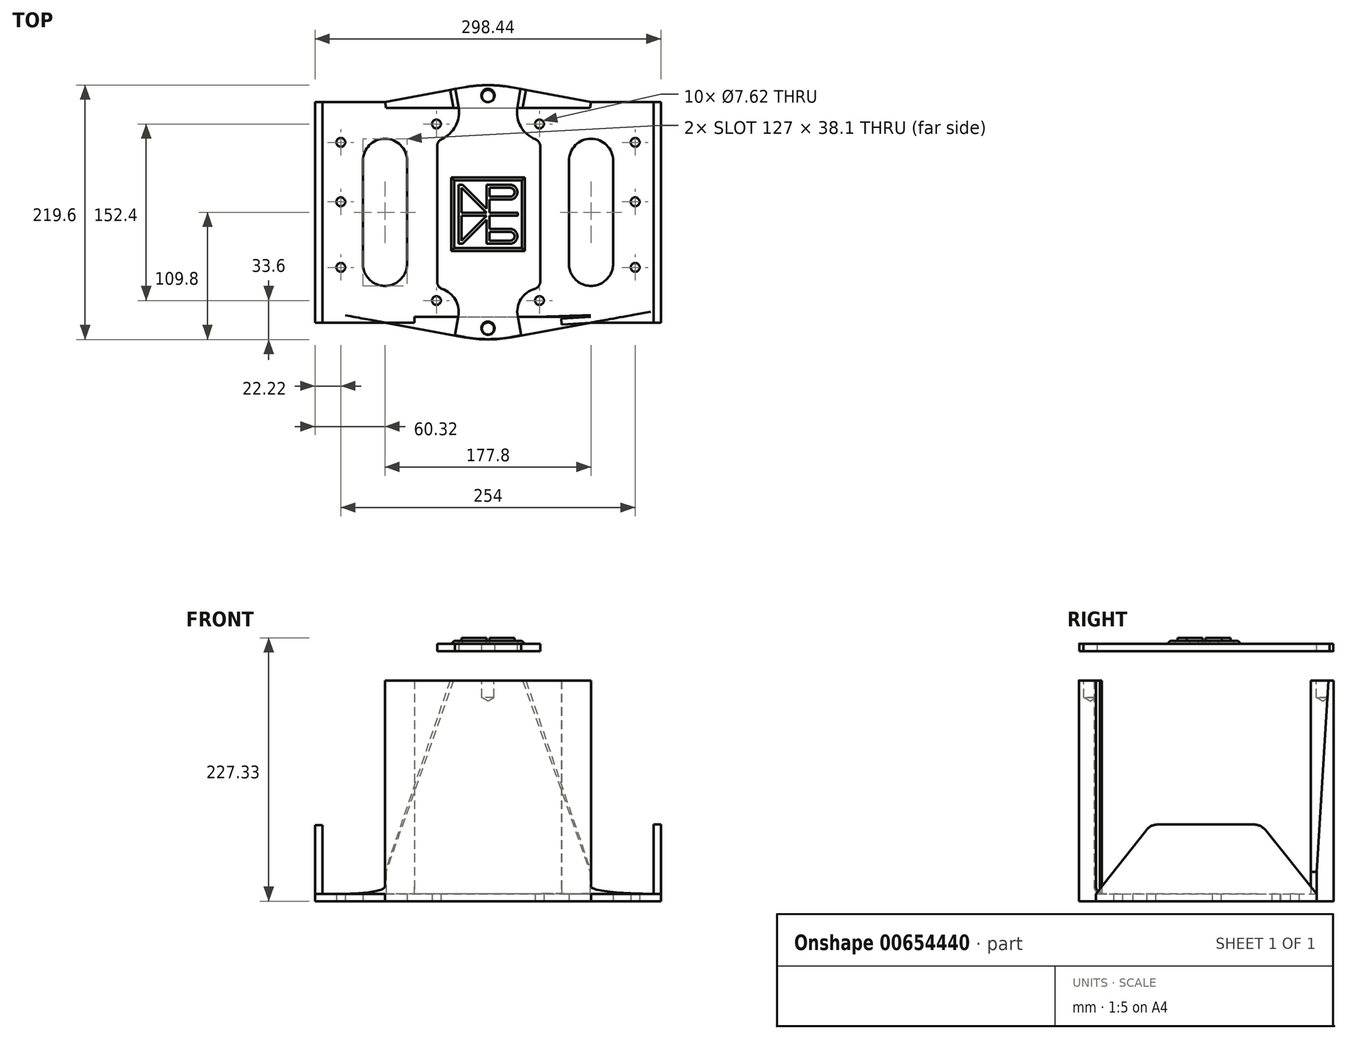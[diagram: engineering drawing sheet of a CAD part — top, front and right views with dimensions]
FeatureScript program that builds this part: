
annotation { "Feature Type Name" : "Feature", "Feature Type Description" : "" }
export const myFeature = defineFeature(function(context is Context, id is Id, definition is map)
    precondition{}
    {
        {
            var Q0;
            Q0=qCreatedBy(makeId("Top.planeOp"),FACE);
            var sketch = newSketch(context, id + "F0", { "sketchPlane" : qUnion([Q0])});
            skLineSegment(sketch, "E0.bottom", {"start": v(-146.05, 86.2) * mm, "end": v(146.05, 86.2) * mm});
            skLineSegment(sketch, "E0.top", {"start": v(-146.05, -104.3) * mm, "end": v(146.05, -104.3) * mm});
            skLineSegment(sketch, "E0.left", {"start": v(-146.05, 86.2) * mm, "end": v(-146.05, -104.3) * mm});
            skLineSegment(sketch, "E0.right", {"start": v(146.05, 86.2) * mm, "end": v(146.05, -104.3) * mm});
            skPoint(sketch, "E1", {"position": v(127, 51.34) * mm});
            skPoint(sketch, "E2", {"position": v(127, -56.61) * mm});
            skPoint(sketch, "E3", {"position": v(127, 0) * mm});
            skPoint(sketch, "E4", {"position": v(-127, 0) * mm});
            skPoint(sketch, "E5", {"position": v(-127, 51.34) * mm});
            skPoint(sketch, "E6", {"position": v(-127, -56.61) * mm});
            skPoint(sketch, "E7", {"position": v(-44.45, 67.14) * mm});
            skPoint(sketch, "E8", {"position": v(44.45, 67.14) * mm});
            skPoint(sketch, "E9", {"position": v(-44.45, -85.26) * mm});
            skPoint(sketch, "E10", {"position": v(44.45, -85.26) * mm});
            skLineSegment(sketch, "E11", {"start": v(-107.95, 35.4) * mm, "end": v(-107.95, -53.5) * mm});
            skLineSegment(sketch, "E12", {"start": v(-69.85, 35.4) * mm, "end": v(-69.85, -53.5) * mm});
            skArc(sketch, "E13", {"start": v(-107.95, 35.4) * mm, "mid": v(-88.9, 54.44) * mm, "end": v(-69.85, 35.4) * mm});
            skArc(sketch, "E14", {"start": v(-107.95, -53.5) * mm, "mid": v(-88.9, -72.56) * mm, "end": v(-69.85, -53.5) * mm});
            skLineSegment(sketch, "E15.MirrorCS", {"start": v(69.85, 35.4) * mm, "end": v(69.85, -53.5) * mm});
            skArc(sketch, "E16.MirrorCS", {"start": v(107.95, 35.4) * mm, "mid": v(88.9, 54.44) * mm, "end": v(69.85, 35.4) * mm});
            skLineSegment(sketch, "E17.MirrorCS", {"start": v(107.95, 35.4) * mm, "end": v(107.95, -53.5) * mm});
            skArc(sketch, "E18.MirrorCS", {"start": v(107.95, -53.5) * mm, "mid": v(88.9, -72.56) * mm, "end": v(69.85, -53.5) * mm});
            skPoint(sketch, "E19", {"position": v(-88.9, 86.2) * mm});
            skPoint(sketch, "E19.positionSnap0", {"position": v(-88.9, 54.44) * mm});
            skPoint(sketch, "E20", {"position": v(-88.9, -104.3) * mm});
            skPoint(sketch, "E20.positionSnap0", {"position": v(-88.9, -72.56) * mm});
            skPoint(sketch, "E21", {"position": v(88.9, 86.2) * mm});
            skPoint(sketch, "E22", {"position": v(88.9, -104.3) * mm});
            skLineSegment(sketch, "E23", {"start": v(-88.9, 86.2) * mm, "end": v(-20.21, 98.9) * mm});
            skLineSegment(sketch, "E24.MirrorCS", {"start": v(88.9, 86.2) * mm, "end": v(20.21, 98.9) * mm});
            skArc(sketch, "E25", {"start": v(-20.21, 98.9) * mm, "mid": v(0, 100.74) * mm, "end": v(20.21, 98.9) * mm});
            skLineSegment(sketch, "E26", {"start": v(-88.9, -104.3) * mm, "end": v(-20.21, -117) * mm});
            skLineSegment(sketch, "E27.MirrorCS", {"start": v(88.9, -104.3) * mm, "end": v(20.21, -117) * mm});
            skArc(sketch, "E28", {"start": v(-20.21, -117) * mm, "mid": v(0, -118.86) * mm, "end": v(20.21, -117) * mm});
            skLineSegment(sketch, "E29", {"start": v(-88.9, -104.3) * mm, "end": v(-88.9, -99.23) * mm});
            skLineSegment(sketch, "E30", {"start": v(-88.9, -99.23) * mm, "end": v(88.59, -99.23) * mm});
            skLineSegment(sketch, "E31", {"start": v(88.59, -99.23) * mm, "end": v(88.9, -104.3) * mm});
            skLineSegment(sketch, "E32", {"start": v(-88.9, 86.2) * mm, "end": v(-88.9, 81.11) * mm});
            skLineSegment(sketch, "E33", {"start": v(-88.9, 81.11) * mm, "end": v(89.2, 81.11) * mm});
            skLineSegment(sketch, "E34", {"start": v(89.2, 81.11) * mm, "end": v(88.9, 86.2) * mm});
            skSolve(sketch);
        }
        {
            var Q0;
            Q0=makeQuery(id+"F0.imprint","IMPRINT",FACE,{"disambiguationData":[TD([[makeQuery(id+"F0.imprint","IMPRINT",EDGE,{"derivedFrom":sQuery(id+"F0.wireOp",EDGE,"E0.bottom")}),-1.0]])]});
            extrude(context, id + "F1", {"entities" : qUnion([Q0]), "depth" : 6.35 * mm, "offsetDistance" : 25.4 * mm});
        }
        {
            var Q0;
            {var subQ0=sQuery(id+"F0.wireOp",EDGE,"E32");Q0=makeQuery(id+"F0.imprint","IMPRINT",FACE,{"disambiguationData":[TD([[makeQuery(id+"F0.imprint","IMPRINT",EDGE,{"derivedFrom":subQ0}),1.0]])]});}
            var Q1;
            {var subQ0=sQuery(id+"F0.wireOp",EDGE,"E23");Q1=makeQuery(id+"F0.imprint","IMPRINT",FACE,{"disambiguationData":[TD([[makeQuery(id+"F0.imprint","IMPRINT",EDGE,{"derivedFrom":subQ0}),-1.0]])]});}
            var Q2;
            {var subQ0=sQuery(id+"F0.wireOp",EDGE,"E29");Q2=makeQuery(id+"F0.imprint","IMPRINT",FACE,{"disambiguationData":[TD([[makeQuery(id+"F0.imprint","IMPRINT",EDGE,{"derivedFrom":subQ0}),-1.0]])]});}
            var Q3;
            {var subQ0=sQuery(id+"F0.wireOp",EDGE,"E26");Q3=makeQuery(id+"F0.imprint","IMPRINT",FACE,{"disambiguationData":[TD([[makeQuery(id+"F0.imprint","IMPRINT",EDGE,{"derivedFrom":subQ0}),1.0]])]});}
            extrude(context, id + "F2", {"entities" : qUnion([Q0, Q1, Q2, Q3]), "operationType" : NewBodyOperationType.ADD, "depth" : 190.5 * mm, "offsetDistance" : 25.4 * mm});
        }
        {
            var Q0;
            Q0=makeQuery(id+"F1.opExtrude","CAP_FACE",FACE,{"disambiguationData":[OSD([sQuery(id+"F0.wireOp",EDGE,"E0.bottom"),sQuery(id+"F0.wireOp",EDGE,"E0.top"),sQuery(id+"F0.wireOp",EDGE,"E0.left"),sQuery(id+"F0.wireOp",EDGE,"E0.right"),sQuery(id+"F0.wireOp",EDGE,"E11"),sQuery(id+"F0.wireOp",EDGE,"E12"),sQuery(id+"F0.wireOp",EDGE,"E13"),sQuery(id+"F0.wireOp",EDGE,"E14"),sQuery(id+"F0.wireOp",EDGE,"E15.MirrorCS"),sQuery(id+"F0.wireOp",EDGE,"E16.MirrorCS"),sQuery(id+"F0.wireOp",EDGE,"E17.MirrorCS"),sQuery(id+"F0.wireOp",EDGE,"E18.MirrorCS")])],"isStart":false});
            var sketch = newSketch(context, id + "F3", { "sketchPlane" : qUnion([Q0])});
            skLineSegment(sketch, "E35.bottom", {"start": v(-140.97, 81.11) * mm, "end": v(140.97, 81.11) * mm});
            skLineSegment(sketch, "E35.top", {"start": v(-140.97, -99.23) * mm, "end": v(140.97, -99.23) * mm});
            skLineSegment(sketch, "E35.left", {"start": v(-140.97, 81.11) * mm, "end": v(-140.97, -99.23) * mm});
            skLineSegment(sketch, "E35.right", {"start": v(140.97, 81.11) * mm, "end": v(140.97, -99.23) * mm});
            skLineSegment(sketch, "E36.bottom", {"start": v(-146.05, 86.2) * mm, "end": v(146.05, 86.2) * mm});
            skLineSegment(sketch, "E36.top", {"start": v(-146.05, -104.3) * mm, "end": v(146.05, -104.3) * mm});
            skLineSegment(sketch, "E36.left", {"start": v(-146.05, 86.2) * mm, "end": v(-146.05, -104.3) * mm});
            skLineSegment(sketch, "E36.right", {"start": v(146.05, 86.2) * mm, "end": v(146.05, -104.3) * mm});
            skSolve(sketch);
        }
        {
            var Q0;
            Q0=makeQuery(id+"F3.imprint","IMPRINT",FACE,{"disambiguationData":[TD([[makeQuery(id+"F3.imprint","IMPRINT",EDGE,{"derivedFrom":sQuery(id+"F3.wireOp",EDGE,"E35.bottom")}),1.0]])]});
            extrude(context, id + "F4", {"entities" : qUnion([Q0]), "operationType" : NewBodyOperationType.ADD, "depth" : 25.4 * mm, "offsetDistance" : 25.4 * mm});
        }
        {
            var Q0;
            Q0=sQuery(id+"F0.wireOp",VERTEX,"E5");
            var Q1;
            Q1=sQuery(id+"F0.wireOp",VERTEX,"E4");
            var Q2;
            Q2=sQuery(id+"F0.wireOp",VERTEX,"E6");
            var Q3;
            Q3=sQuery(id+"F0.wireOp",VERTEX,"E9");
            var Q4;
            Q4=sQuery(id+"F0.wireOp",VERTEX,"E10");
            var Q5;
            Q5=sQuery(id+"F0.wireOp",VERTEX,"E2");
            var Q6;
            Q6=sQuery(id+"F0.wireOp",VERTEX,"E3");
            var Q7;
            Q7=sQuery(id+"F0.wireOp",VERTEX,"E1");
            var Q8;
            Q8=sQuery(id+"F0.wireOp",VERTEX,"E8");
            var Q9;
            Q9=sQuery(id+"F0.wireOp",VERTEX,"E7");
            var Q10;
            Q10=makeQuery(id+"F1.opExtrude","SWEPT_BODY",BODY,{"disambiguationData":[OSD([sQuery(id+"F0.wireOp",EDGE,"E0.bottom"),sQuery(id+"F0.wireOp",EDGE,"E0.top"),sQuery(id+"F0.wireOp",EDGE,"E0.left"),sQuery(id+"F0.wireOp",EDGE,"E0.right"),sQuery(id+"F0.wireOp",EDGE,"E11"),sQuery(id+"F0.wireOp",EDGE,"E12"),sQuery(id+"F0.wireOp",EDGE,"E13"),sQuery(id+"F0.wireOp",EDGE,"E14"),sQuery(id+"F0.wireOp",EDGE,"E15.MirrorCS"),sQuery(id+"F0.wireOp",EDGE,"E16.MirrorCS"),sQuery(id+"F0.wireOp",EDGE,"E17.MirrorCS"),sQuery(id+"F0.wireOp",EDGE,"E18.MirrorCS")])]});
            hole(context, id + "F5", {"style" : HoleStyle.SIMPLE, "endStyle" : HoleEndStyle.THROUGH, "oppositeDirection" : true, "holeDiameter" : 7.62 * mm, "majorDiameter" : 6.35 * mm, "isTappedThrough" : true, "tappedDepth" : 10.16 * mm, "tapClearance" : 3, "locations" : qUnion([Q0, Q1, Q2, Q3, Q4, Q5, Q6, Q7, Q8, Q9]), "scope" : qUnion([Q10])});
        }
        {
            var Q0;
            Q0=makeQuery(id+"F2.opExtrude","SWEPT_FACE",FACE,{"disambiguationData":[OSD([sQuery(id+"F0.wireOp",EDGE,"E26")])]});
            var sketch = newSketch(context, id + "F6", { "sketchPlane" : qUnion([Q0])});
            skLineSegment(sketch, "E37", {"start": v(-68.45, 25.4) * mm, "end": v(-11.3, 190.5) * mm});
            skSolve(sketch);
        }
        {
            var Q0;
            Q0 = qSketchRegion(id + "F6", true);
            var Q1;
            {var subQ0=sQuery(id+"F6.wireOp",EDGE,"E37");Q1=makeQuery(id+"F6.imprint","IMPRINT",FACE,{"disambiguationData":[TD([[makeQuery(id+"F6.imprint","IMPRINT",EDGE,{"derivedFrom":subQ0}),1.0]])]});}
            var Q2;
            Q2=makeQuery(id+"F2.opExtrude","SWEPT_FACE",FACE,{"disambiguationData":[OSD([sQuery(id+"F0.wireOp",EDGE,"E29")])]});
            extrude(context, id + "F7", {"entities" : qUnion([Q0, Q1, Q2]), "operationType" : NewBodyOperationType.REMOVE, "oppositeDirection" : true, "depth" : 25.4 * mm, "offsetDistance" : 25.4 * mm});
        }
        {
            var Q0;
            Q0=makeQuery(id+"F2.opExtrude","SWEPT_FACE",FACE,{"disambiguationData":[OSD([sQuery(id+"F0.wireOp",EDGE,"E27.MirrorCS")])]});
            var sketch = newSketch(context, id + "F8", { "sketchPlane" : qUnion([Q0])});
            skLineSegment(sketch, "E38", {"start": v(11.3, 190.5) * mm, "end": v(68.45, 25.4) * mm});
            skSolve(sketch);
        }
        {
            var Q0;
            Q0 = qSketchRegion(id + "F8", true);
            var Q1;
            {var subQ0=sQuery(id+"F8.wireOp",EDGE,"E38");Q1=makeQuery(id+"F8.imprint","IMPRINT",FACE,{"disambiguationData":[TD([[makeQuery(id+"F8.imprint","IMPRINT",EDGE,{"derivedFrom":subQ0}),1.0]])]});}
            var Q2;
            Q2=makeQuery(id+"F2.opExtrude","SWEPT_FACE",FACE,{"disambiguationData":[OSD([sQuery(id+"F0.wireOp",EDGE,"E31")])]});
            extrude(context, id + "F9", {"entities" : qUnion([Q0, Q1, Q2]), "operationType" : NewBodyOperationType.REMOVE, "oppositeDirection" : true, "depth" : 25.4 * mm, "offsetDistance" : 25.4 * mm});
        }
        {
            var Q0;
            Q0=makeQuery(id+"F2.opExtrude","SWEPT_FACE",FACE,{"disambiguationData":[OSD([sQuery(id+"F0.wireOp",EDGE,"E24.MirrorCS")])]});
            var sketch = newSketch(context, id + "F10", { "sketchPlane" : qUnion([Q0])});
            skLineSegment(sketch, "E39", {"start": v(-14.6, 190.5) * mm, "end": v(-71.75, 25.4) * mm});
            skSolve(sketch);
        }
        {
            var Q0;
            Q0 = qSketchRegion(id + "F10", true);
            var Q1;
            {var subQ0=sQuery(id+"F10.wireOp",EDGE,"E39");Q1=makeQuery(id+"F10.imprint","IMPRINT",FACE,{"disambiguationData":[TD([[makeQuery(id+"F10.imprint","IMPRINT",EDGE,{"derivedFrom":subQ0}),-1.0]])]});}
            var Q2;
            Q2=makeQuery(id+"F2.opExtrude","SWEPT_FACE",FACE,{"disambiguationData":[OSD([sQuery(id+"F0.wireOp",EDGE,"E34")])]});
            extrude(context, id + "F11", {"entities" : qUnion([Q0, Q1, Q2]), "operationType" : NewBodyOperationType.REMOVE, "oppositeDirection" : true, "depth" : 25.4 * mm, "offsetDistance" : 25.4 * mm});
        }
        {
            var Q0;
            Q0=makeQuery(id+"F2.opExtrude","SWEPT_FACE",FACE,{"disambiguationData":[OSD([sQuery(id+"F0.wireOp",EDGE,"E23")])]});
            var sketch = newSketch(context, id + "F12", { "sketchPlane" : qUnion([Q0])});
            skLineSegment(sketch, "E40", {"start": v(14.6, 190.5) * mm, "end": v(71.75, 25.4) * mm});
            skSolve(sketch);
        }
        {
            var Q0;
            Q0 = qSketchRegion(id + "F12", true);
            var Q1;
            {var subQ0=sQuery(id+"F12.wireOp",EDGE,"E40");Q1=makeQuery(id+"F12.imprint","IMPRINT",FACE,{"disambiguationData":[TD([[makeQuery(id+"F12.imprint","IMPRINT",EDGE,{"derivedFrom":subQ0}),1.0]])]});}
            var Q2;
            Q2=makeQuery(id+"F2.opExtrude","SWEPT_FACE",FACE,{"disambiguationData":[OSD([sQuery(id+"F0.wireOp",EDGE,"E32")])]});
            extrude(context, id + "F13", {"entities" : qUnion([Q0, Q1, Q2]), "operationType" : NewBodyOperationType.REMOVE, "oppositeDirection" : true, "depth" : 25.4 * mm, "offsetDistance" : 25.4 * mm});
        }
        {
            var Q0;
            Q0=makeQuery(id+"F1.opExtrude","SWEPT_FACE",FACE,{"disambiguationData":[OSD([sQuery(id+"F0.wireOp",EDGE,"E0.left")])]});
            var sketch = newSketch(context, id + "F14", { "sketchPlane" : qUnion([Q0])});
            skLineSegment(sketch, "E41", {"start": v(-86.2, 0) * mm, "end": v(-86.2, 6.35) * mm});
            skLineSegment(sketch, "E42", {"start": v(-86.2, 6.35) * mm, "end": v(-42.22, 60.97) * mm});
            skLineSegment(sketch, "E43", {"start": v(-32.33, 65.7) * mm, "end": v(50.74, 65.7) * mm});
            skLineSegment(sketch, "E44", {"start": v(60.65, 60.94) * mm, "end": v(104.3, 6.35) * mm});
            skLineSegment(sketch, "E45", {"start": v(104.3, 6.35) * mm, "end": v(104.3, 0) * mm});
            skLineSegment(sketch, "E46", {"start": v(104.3, 0) * mm, "end": v(-86.2, 0) * mm});
            skPoint(sketch, "E47.visualSharp", {"position": v(-38.4, 65.7) * mm});
            skArc(sketch, "E47.filletArc", {"start": v(-32.33, 65.7) * mm, "mid": v(-37.81, 64.46) * mm, "end": v(-42.22, 60.97) * mm});
            skPoint(sketch, "E48.visualSharp", {"position": v(56.84, 65.7) * mm});
            skArc(sketch, "E48.filletArc", {"start": v(60.65, 60.94) * mm, "mid": v(56.24, 64.45) * mm, "end": v(50.74, 65.7) * mm});
            skSolve(sketch);
        }
        {
            var Q0;
            Q0 = qSketchRegion(id + "F14", true);
            extrude(context, id + "F15", {"entities" : qUnion([Q0]), "operationType" : NewBodyOperationType.ADD, "endBound" : BoundingType.SYMMETRIC, "depth" : 6.35 * mm, "offsetDistance" : 25.4 * mm});
        }
        {
            var Q0;
            Q0=makeQuery(id+"F1.opExtrude","SWEPT_FACE",FACE,{"disambiguationData":[OSD([sQuery(id+"F0.wireOp",EDGE,"E0.right")])]});
            var sketch = newSketch(context, id + "F16", { "sketchPlane" : qUnion([Q0])});
            skLineSegment(sketch, "E49", {"start": v(-104.3, 0) * mm, "end": v(-104.3, 6.35) * mm});
            skLineSegment(sketch, "E50", {"start": v(-104.3, 6.35) * mm, "end": v(-60.88, 61.31) * mm});
            skLineSegment(sketch, "E51", {"start": v(-50.92, 66.14) * mm, "end": v(32.09, 66.14) * mm});
            skLineSegment(sketch, "E52", {"start": v(42, 61.4) * mm, "end": v(86.2, 6.35) * mm});
            skLineSegment(sketch, "E53", {"start": v(86.2, 6.35) * mm, "end": v(86.2, 0) * mm});
            skLineSegment(sketch, "E54", {"start": v(86.2, 0) * mm, "end": v(-104.3, 0) * mm});
            skPoint(sketch, "E55.visualSharp", {"position": v(-57.07, 66.14) * mm});
            skArc(sketch, "E55.filletArc", {"start": v(-50.92, 66.14) * mm, "mid": v(-56.46, 64.87) * mm, "end": v(-60.88, 61.31) * mm});
            skPoint(sketch, "E56.visualSharp", {"position": v(38.18, 66.14) * mm});
            skArc(sketch, "E56.filletArc", {"start": v(42, 61.4) * mm, "mid": v(37.58, 64.9) * mm, "end": v(32.09, 66.14) * mm});
            skSolve(sketch);
        }
        {
            var Q0;
            Q0 = qSketchRegion(id + "F16", true);
            extrude(context, id + "F17", {"entities" : qUnion([Q0]), "operationType" : NewBodyOperationType.ADD, "endBound" : BoundingType.SYMMETRIC, "depth" : 6.35 * mm, "offsetDistance" : 25.4 * mm});
        }
        {
            var Q0;
            Q0=makeQuery(id+"F7.boolean.opBoolean","COPY",EDGE,{"derivedFrom":makeQuery(id+"F7.opExtrude","CAP_EDGE",EDGE,{"disambiguationData":[OSD([sQuery(id+"F6.wireOp",EDGE,"E37")])],"isStart":true})});
            var Q1;
            Q1=makeQuery(id+"F9.boolean.opBoolean","COPY",EDGE,{"derivedFrom":makeQuery(id+"F9.opExtrude","CAP_EDGE",EDGE,{"disambiguationData":[OSD([sQuery(id+"F8.wireOp",EDGE,"E38")])],"isStart":true})});
            var Q2;
            Q2=makeQuery(id+"F9.boolean.opBoolean","COPY",EDGE,{"derivedFrom":makeQuery(id+"F9.opExtrude","SWEPT_EDGE",EDGE,{"disambiguationData":[OSD([sQuery(id+"F0.wireOp",EDGE,"E27.MirrorCS"),sQuery(id+"F8.wireOp",EDGE,"E38")])]})});
            var Q3;
            Q3=makeQuery(id+"F7.boolean.opBoolean","COPY",EDGE,{"derivedFrom":makeQuery(id+"F7.opExtrude","SWEPT_EDGE",EDGE,{"disambiguationData":[OSD([sQuery(id+"F0.wireOp",EDGE,"E26"),sQuery(id+"F6.wireOp",EDGE,"E37")])]})});
            var Q4;
            Q4=makeQuery(id+"F11.boolean.opBoolean","COPY",EDGE,{"derivedFrom":makeQuery(id+"F11.opExtrude","CAP_EDGE",EDGE,{"disambiguationData":[OSD([sQuery(id+"F10.wireOp",EDGE,"E39")])],"isStart":true})});
            var Q5;
            Q5=makeQuery(id+"F13.boolean.opBoolean","COPY",EDGE,{"derivedFrom":makeQuery(id+"F13.opExtrude","CAP_EDGE",EDGE,{"disambiguationData":[OSD([sQuery(id+"F12.wireOp",EDGE,"E40")])],"isStart":true})});
            var Q6;
            Q6=makeQuery(id+"F11.boolean.opBoolean","COPY",EDGE,{"derivedFrom":makeQuery(id+"F11.opExtrude","SWEPT_EDGE",EDGE,{"disambiguationData":[OSD([sQuery(id+"F0.wireOp",EDGE,"E24.MirrorCS"),sQuery(id+"F10.wireOp",EDGE,"E39")])]})});
            var Q7;
            Q7=makeQuery(id+"F13.boolean.opBoolean","COPY",EDGE,{"derivedFrom":makeQuery(id+"F13.opExtrude","SWEPT_EDGE",EDGE,{"disambiguationData":[OSD([sQuery(id+"F0.wireOp",EDGE,"E23"),sQuery(id+"F12.wireOp",EDGE,"E40")])]})});
            fillet(context, id + "F18", {"entities" : qUnion([Q0, Q1, Q2, Q3, Q4, Q5, Q6, Q7]), "radius" : 6.35 * mm, "tangentPropagation" : true, "allowEdgeOverflow" : false});
        }
        {
            var Q0;
            Q0=makeQuery(id+"F2.opExtrude","CAP_FACE",FACE,{"disambiguationData":[OSD([sQuery(id+"F0.wireOp",EDGE,"E23"),sQuery(id+"F0.wireOp",EDGE,"E24.MirrorCS"),sQuery(id+"F0.wireOp",EDGE,"E25"),sQuery(id+"F0.wireOp",EDGE,"E32"),sQuery(id+"F0.wireOp",EDGE,"E33"),sQuery(id+"F0.wireOp",EDGE,"E34")])],"isStart":false});
            var sketch = newSketch(context, id + "F19", { "sketchPlane" : qUnion([Q0])});
            skPoint(sketch, "E57", {"position": v(0, 91.27) * mm});
            skPoint(sketch, "E58", {"position": v(0, -109.39) * mm});
            skLineSegment(sketch, "E59", {"start": v(-20.21, 98.9) * mm, "end": v(-20.21, 81.11) * mm});
            skLineSegment(sketch, "E60", {"start": v(20.21, 98.9) * mm, "end": v(20.21, 81.11) * mm});
            skLineSegment(sketch, "E61", {"start": v(-20.21, 98.9) * mm, "end": v(20.21, 98.9) * mm});
            skLineSegment(sketch, "E62", {"start": v(20.21, 81.11) * mm, "end": v(-20.21, 81.11) * mm});
            skSolve(sketch);
        }
        {
            var Q0;
            Q0=sQuery(id+"F19.wireOp",VERTEX,"E57");
            var Q1;
            Q1=sQuery(id+"F19.wireOp",VERTEX,"E58");
            var Q2;
            Q2=makeQuery(id+"F1.opExtrude","SWEPT_BODY",BODY,{"disambiguationData":[OSD([sQuery(id+"F0.wireOp",EDGE,"E0.bottom"),sQuery(id+"F0.wireOp",EDGE,"E0.top"),sQuery(id+"F0.wireOp",EDGE,"E0.left"),sQuery(id+"F0.wireOp",EDGE,"E0.right"),sQuery(id+"F0.wireOp",EDGE,"E11"),sQuery(id+"F0.wireOp",EDGE,"E12"),sQuery(id+"F0.wireOp",EDGE,"E13"),sQuery(id+"F0.wireOp",EDGE,"E14"),sQuery(id+"F0.wireOp",EDGE,"E15.MirrorCS"),sQuery(id+"F0.wireOp",EDGE,"E16.MirrorCS"),sQuery(id+"F0.wireOp",EDGE,"E17.MirrorCS"),sQuery(id+"F0.wireOp",EDGE,"E18.MirrorCS"),sQuery(id+"F0.wireOp",EDGE,"E29"),sQuery(id+"F0.wireOp",EDGE,"E30"),sQuery(id+"F0.wireOp",EDGE,"E31"),sQuery(id+"F0.wireOp",EDGE,"E32"),sQuery(id+"F0.wireOp",EDGE,"E33"),sQuery(id+"F0.wireOp",EDGE,"E34")])]});
            hole(context, id + "F20", {"style" : HoleStyle.SIMPLE, "endStyle" : HoleEndStyle.BLIND, "standardTappedOrClearance" : lookupTablePath({ "standard" : "ISO", "engagement" : "75%", "pitch" : "1.5 mm", "size" : "M12", "type" : "Tapped" }), "standardBlindInLast" : lookupTablePath({ "standard" : "ISO", "engagement" : "75%", "pitch" : "1.5 mm", "size" : "M12", "type" : "Tapped" }), "holeDiameter" : 10.5 * mm, "majorDiameter" : 12 * mm, "showTappedDepth" : true, "holeDepth" : 14.66 * mm, "isTappedThrough" : true, "tappedDepth" : 10.16 * mm, "tapClearance" : 3, "locations" : qUnion([Q0, Q1]), "scope" : qUnion([Q2])});
        }
        {
            var Q0;
            Q0=makeQuery(id+"F2.opExtrude","CAP_FACE",FACE,{"disambiguationData":[OSD([sQuery(id+"F0.wireOp",EDGE,"E23"),sQuery(id+"F0.wireOp",EDGE,"E24.MirrorCS"),sQuery(id+"F0.wireOp",EDGE,"E25"),sQuery(id+"F0.wireOp",EDGE,"E32"),sQuery(id+"F0.wireOp",EDGE,"E33"),sQuery(id+"F0.wireOp",EDGE,"E34")])],"isStart":false});
            cPlane(context, id + "F21", {"entities" : qUnion([Q0]), "cplaneType" : CPlaneType.OFFSET, "offset" : 25.4 * mm, "width" : 152.4 * mm, "height" : 152.4 * mm});
        }
        {
            var Q0;
            Q0=qCreatedBy(id+"F21.planeOp",FACE);
            var sketch = newSketch(context, id + "F22", { "sketchPlane" : qUnion([Q0])});
            skLineSegment(sketch, "E63", {"start": v(-28.14, 97.53) * mm, "end": v(-25.4, 81.65) * mm});
            skLineSegment(sketch, "E64", {"start": v(-28.14, 97.53) * mm, "end": v(-20.57, 98.84) * mm});
            skLineSegment(sketch, "E65", {"start": v(0, 102.68) * mm, "end": v(0, 80.93) * mm});
            skLineSegment(sketch, "E66.MirrorCS", {"start": v(28.14, 97.53) * mm, "end": v(20.57, 98.84) * mm});
            skLineSegment(sketch, "E67.MirrorCS", {"start": v(28.14, 97.53) * mm, "end": v(25.4, 81.65) * mm});
            skArc(sketch, "E68", {"start": v(-20.57, 98.84) * mm, "mid": v(0, 100.6) * mm, "end": v(20.57, 98.84) * mm});
            skLineSegment(sketch, "E69", {"start": v(-25.62, -98.93) * mm, "end": v(-28.66, -115.17) * mm});
            skLineSegment(sketch, "E70", {"start": v(-28.66, -115.17) * mm, "end": v(-21.2, -116.56) * mm});
            skLineSegment(sketch, "E71", {"start": v(0, -96.58) * mm, "end": v(0, -121.6) * mm});
            skLineSegment(sketch, "E72.MirrorCS", {"start": v(25.62, -98.93) * mm, "end": v(28.66, -115.17) * mm});
            skLineSegment(sketch, "E73.MirrorCS", {"start": v(28.66, -115.17) * mm, "end": v(21.2, -116.56) * mm});
            skArc(sketch, "E74", {"start": v(-21.2, -116.56) * mm, "mid": v(0, -118.52) * mm, "end": v(21.2, -116.56) * mm});
            skLineSegment(sketch, "E75.bottom", {"start": v(-43.83, 52.72) * mm, "end": v(45.07, 52.72) * mm});
            skLineSegment(sketch, "E75.top", {"start": v(-43.83, -74.28) * mm, "end": v(45.07, -74.28) * mm});
            skLineSegment(sketch, "E75.left", {"start": v(-43.83, 52.72) * mm, "end": v(-43.83, -74.28) * mm});
            skLineSegment(sketch, "E75.right", {"start": v(45.07, 52.72) * mm, "end": v(45.07, -74.28) * mm});
            skArc(sketch, "E76", {"start": v(-25.62, -98.93) * mm, "mid": v(-29.36, -82.64) * mm, "end": v(-43.83, -74.28) * mm});
            skArc(sketch, "E77", {"start": v(25.62, -98.93) * mm, "mid": v(29.75, -82.19) * mm, "end": v(45.07, -74.28) * mm});
            skArc(sketch, "E78", {"start": v(-25.4, 81.65) * mm, "mid": v(-29.01, 63.61) * mm, "end": v(-43.83, 52.72) * mm});
            skArc(sketch, "E79", {"start": v(25.4, 81.65) * mm, "mid": v(29.38, 63.2) * mm, "end": v(45.07, 52.72) * mm});
            skPoint(sketch, "E80", {"position": v(0, 91.8) * mm});
            skPoint(sketch, "E81", {"position": v(0, -109.09) * mm});
            skLineSegment(sketch, "E82", {"start": v(-25.4, 81.65) * mm, "end": v(25.4, 81.65) * mm});
            skLineSegment(sketch, "E83", {"start": v(-25.62, -98.93) * mm, "end": v(25.62, -98.93) * mm});
            skSolve(sketch);
        }
        {
            var Q0;
            Q0 = qSketchRegion(id + "F22", true);
            extrude(context, id + "F23", {"entities" : qUnion([Q0]), "depth" : 6.35 * mm, "offsetDistance" : 25.4 * mm});
        }
        {
            var Q0;
            Q0=makeQuery(id+"F23.opExtrude","SWEPT_EDGE",EDGE,{"disambiguationData":[OSD([sQuery(id+"F22.wireOp",EDGE,"E75.bottom"),sQuery(id+"F22.wireOp",EDGE,"E75.left"),sQuery(id+"F22.wireOp",EDGE,"E78")])]});
            var Q1;
            Q1=makeQuery(id+"F23.opExtrude","SWEPT_EDGE",EDGE,{"disambiguationData":[OSD([sQuery(id+"F22.wireOp",EDGE,"E75.top"),sQuery(id+"F22.wireOp",EDGE,"E75.left"),sQuery(id+"F22.wireOp",EDGE,"E76")])]});
            var Q2;
            Q2=makeQuery(id+"F23.opExtrude","SWEPT_EDGE",EDGE,{"disambiguationData":[OSD([sQuery(id+"F22.wireOp",EDGE,"E75.bottom"),sQuery(id+"F22.wireOp",EDGE,"E75.right"),sQuery(id+"F22.wireOp",EDGE,"E79")])]});
            var Q3;
            Q3=makeQuery(id+"F23.opExtrude","SWEPT_EDGE",EDGE,{"disambiguationData":[OSD([sQuery(id+"F22.wireOp",EDGE,"E75.top"),sQuery(id+"F22.wireOp",EDGE,"E75.right"),sQuery(id+"F22.wireOp",EDGE,"E77")])]});
            fillet(context, id + "F24", {"entities" : qUnion([Q0, Q1, Q2, Q3]), "radius" : 6.35 * mm, "tangentPropagation" : true, "allowEdgeOverflow" : false});
        }
        {
            var Q0;
            Q0=sQuery(id+"F22.wireOp",VERTEX,"E81");
            var Q1;
            Q1=sQuery(id+"F22.wireOp",VERTEX,"E80");
            var Q2;
            Q2=makeQuery(id+"F23.opExtrude","SWEPT_BODY",BODY,{"disambiguationData":[OSD([sQuery(id+"F22.wireOp",EDGE,"E63"),sQuery(id+"F22.wireOp",EDGE,"E64"),sQuery(id+"F22.wireOp",EDGE,"E66.MirrorCS"),sQuery(id+"F22.wireOp",EDGE,"E67.MirrorCS"),sQuery(id+"F22.wireOp",EDGE,"E68"),sQuery(id+"F22.wireOp",EDGE,"E69"),sQuery(id+"F22.wireOp",EDGE,"E70"),sQuery(id+"F22.wireOp",EDGE,"E72.MirrorCS"),sQuery(id+"F22.wireOp",EDGE,"E73.MirrorCS"),sQuery(id+"F22.wireOp",EDGE,"E74"),sQuery(id+"F22.wireOp",EDGE,"E75.left"),sQuery(id+"F22.wireOp",EDGE,"E75.right"),sQuery(id+"F22.wireOp",EDGE,"E76"),sQuery(id+"F22.wireOp",EDGE,"E77"),sQuery(id+"F22.wireOp",EDGE,"E78"),sQuery(id+"F22.wireOp",EDGE,"E79")])]});
            hole(context, id + "F25", {"style" : HoleStyle.SIMPLE, "endStyle" : HoleEndStyle.BLIND, "oppositeDirection" : true, "holeDiameter" : 11.43 * mm, "majorDiameter" : 6.35 * mm, "holeDepth" : 6.35 * mm, "isTappedThrough" : true, "tappedDepth" : 10.16 * mm, "tapClearance" : 3, "locations" : qUnion([Q0, Q1]), "scope" : qUnion([Q2])});
        }
        {
            var Q0;
            Q0=makeQuery(id+"F23.opExtrude","CAP_FACE",FACE,{"disambiguationData":[OSD([sQuery(id+"F22.wireOp",EDGE,"E63"),sQuery(id+"F22.wireOp",EDGE,"E64"),sQuery(id+"F22.wireOp",EDGE,"E66.MirrorCS"),sQuery(id+"F22.wireOp",EDGE,"E67.MirrorCS"),sQuery(id+"F22.wireOp",EDGE,"E68"),sQuery(id+"F22.wireOp",EDGE,"E69"),sQuery(id+"F22.wireOp",EDGE,"E70"),sQuery(id+"F22.wireOp",EDGE,"E72.MirrorCS"),sQuery(id+"F22.wireOp",EDGE,"E73.MirrorCS"),sQuery(id+"F22.wireOp",EDGE,"E74"),sQuery(id+"F22.wireOp",EDGE,"E75.left"),sQuery(id+"F22.wireOp",EDGE,"E75.right"),sQuery(id+"F22.wireOp",EDGE,"E76"),sQuery(id+"F22.wireOp",EDGE,"E77"),sQuery(id+"F22.wireOp",EDGE,"E78"),sQuery(id+"F22.wireOp",EDGE,"E79")])],"isStart":false});
            var sketch = newSketch(context, id + "F26", { "sketchPlane" : qUnion([Q0])});
            skPoint(sketch, "E84.startSnap0", {"position": v(0, -10.72) * mm});
            skPoint(sketch, "E84.startSnap1", {"position": v(-43.83, -10.48) * mm});
            skLineSegment(sketch, "E85.bottom", {"start": v(-31.75, 21.03) * mm, "end": v(31.75, 21.03) * mm});
            skLineSegment(sketch, "E85.top", {"start": v(-31.75, -42.47) * mm, "end": v(31.75, -42.47) * mm});
            skLineSegment(sketch, "E85.left", {"start": v(-31.75, 21.03) * mm, "end": v(-31.75, -42.47) * mm});
            skLineSegment(sketch, "E85.right", {"start": v(31.75, 21.03) * mm, "end": v(31.75, -42.47) * mm});
            skLineSegment(sketch, "E86", {"start": v(-25.4, 14.68) * mm, "end": v(-25.4, -36.12) * mm});
            skLineSegment(sketch, "E87", {"start": v(-25.4, 14.68) * mm, "end": v(0, -10.72) * mm});
            skLineSegment(sketch, "E88", {"start": v(-25.4, -36.12) * mm, "end": v(0, -10.72) * mm});
            skLineSegment(sketch, "E89", {"start": v(0, 14.68) * mm, "end": v(19.03, 14.68) * mm});
            skLineSegment(sketch, "E90", {"start": v(0, 1.93) * mm, "end": v(19.03, 1.93) * mm});
            skArc(sketch, "E91", {"start": v(19.03, 14.68) * mm, "mid": v(25.4, 8.3) * mm, "end": v(19.03, 1.93) * mm});
            skLineSegment(sketch, "E92.MirrorCS", {"start": v(0, -23.38) * mm, "end": v(19.03, -23.38) * mm});
            skArc(sketch, "E93.MirrorCS", {"start": v(19.03, -36.12) * mm, "mid": v(25.4, -29.75) * mm, "end": v(19.03, -23.38) * mm});
            skLineSegment(sketch, "E94.MirrorCS", {"start": v(0, -36.12) * mm, "end": v(19.03, -36.12) * mm});
            skLineSegment(sketch, "E95", {"start": v(0, 14.68) * mm, "end": v(0, -36.12) * mm});
            skLineSegment(sketch, "E96", {"start": v(25.4, -10.72) * mm, "end": v(-25.4, -10.72) * mm});
            skPoint(sketch, "E96.startSnap0", {"position": v(25.4, 8.3) * mm});
            skSolve(sketch);
        }
        {
            var Q0;
            Q0=makeQuery(id+"F26.imprint","IMPRINT",FACE,{"disambiguationData":[TD([[makeQuery(id+"F26.imprint","IMPRINT",EDGE,{"derivedFrom":sQuery(id+"F26.wireOp",EDGE,"E85.bottom")}),-1.0]])]});
            var Q1;
            Q1=sQuery(id+"F26.wireOp",EDGE,"E85.right");
            var Q2;
            Q2=sQuery(id+"F26.wireOp",EDGE,"E85.bottom");
            var Q3;
            Q3=sQuery(id+"F26.wireOp",EDGE,"E85.left");
            var Q4;
            Q4=sQuery(id+"F26.wireOp",EDGE,"E96");
            var Q5;
            Q5=sQuery(id+"F26.wireOp",EDGE,"E95");
            var Q6;
            Q6=sQuery(id+"F26.wireOp",EDGE,"E87");
            var Q7;
            Q7=sQuery(id+"F26.wireOp",EDGE,"E86");
            var Q8;
            Q8=sQuery(id+"F26.wireOp",EDGE,"E88");
            var Q9;
            Q9=sQuery(id+"F26.wireOp",EDGE,"E94.MirrorCS");
            var Q10;
            Q10=sQuery(id+"F26.wireOp",EDGE,"E92.MirrorCS");
            var Q11;
            Q11=sQuery(id+"F26.wireOp",EDGE,"E93.MirrorCS");
            var Q12;
            Q12=sQuery(id+"F26.wireOp",EDGE,"E90");
            var Q13;
            Q13=sQuery(id+"F26.wireOp",EDGE,"E91");
            var Q14;
            Q14=sQuery(id+"F26.wireOp",EDGE,"E89");
            var Q15;
            Q15=sQuery(id+"F26.wireOp",EDGE,"E85.top");
            extrude(context, id + "F27", {"entities" : qUnion([Q0]), "surfaceEntities" : qUnion([Q1, Q2, Q3, Q4, Q5, Q6, Q7, Q8, Q9, Q10, Q11, Q12, Q13, Q14, Q15]), "depth" : 2.54 * mm, "offsetDistance" : 25.4 * mm});
        }
        {
            var Q0;
            Q0=makeQuery(id+"F27.opExtrude","CAP_FACE",FACE,{"disambiguationData":[OSD([sQuery(id+"F26.wireOp",EDGE,"E85.bottom"),sQuery(id+"F26.wireOp",EDGE,"E85.top"),sQuery(id+"F26.wireOp",EDGE,"E85.left"),sQuery(id+"F26.wireOp",EDGE,"E85.right"),sQuery(id+"F26.wireOp",EDGE,"E86"),sQuery(id+"F26.wireOp",EDGE,"E87"),sQuery(id+"F26.wireOp",EDGE,"E88"),sQuery(id+"F26.wireOp",EDGE,"E89"),sQuery(id+"F26.wireOp",EDGE,"E90"),sQuery(id+"F26.wireOp",EDGE,"E91"),sQuery(id+"F26.wireOp",EDGE,"E92.MirrorCS"),sQuery(id+"F26.wireOp",EDGE,"E93.MirrorCS"),sQuery(id+"F26.wireOp",EDGE,"E94.MirrorCS"),sQuery(id+"F26.wireOp",EDGE,"E95")])],"isStart":false});
            var sketch = newSketch(context, id + "F28", { "sketchPlane" : qUnion([Q0])});
            skLineSegment(sketch, "E97", {"start": v(-25.4, -9.45) * mm, "end": v(-1.27, -9.45) * mm});
            skLineSegment(sketch, "E98", {"start": v(-1.27, -9.45) * mm, "end": v(0, -10.72) * mm});
            skLineSegment(sketch, "E99", {"start": v(0, -10.72) * mm, "end": v(-1.27, -12) * mm});
            skLineSegment(sketch, "E100", {"start": v(-1.27, -12) * mm, "end": v(-25.4, -12) * mm});
            skLineSegment(sketch, "E101", {"start": v(-25.4, -12) * mm, "end": v(-25.4, -9.45) * mm});
            skLineSegment(sketch, "E102", {"start": v(-1.27, -9.45) * mm, "end": v(25.73, -9.45) * mm});
            skLineSegment(sketch, "E103", {"start": v(25.73, -9.45) * mm, "end": v(25.73, -12) * mm});
            skLineSegment(sketch, "E104", {"start": v(25.73, -12) * mm, "end": v(-1.27, -12) * mm});
            skLineSegment(sketch, "E105", {"start": v(0, -36.12) * mm, "end": v(1.27, -36.12) * mm});
            skLineSegment(sketch, "E106", {"start": v(1.27, -36.12) * mm, "end": v(1.27, 14.68) * mm});
            skLineSegment(sketch, "E107", {"start": v(1.27, 14.68) * mm, "end": v(0, 14.68) * mm});
            skLineSegment(sketch, "E108.MirrorCS", {"start": v(-1.27, -36.12) * mm, "end": v(-1.27, 14.68) * mm});
            skLineSegment(sketch, "E109.MirrorCS", {"start": v(-1.27, 14.68) * mm, "end": v(0, 14.68) * mm});
            skLineSegment(sketch, "E110.MirrorCS", {"start": v(0, -36.12) * mm, "end": v(-1.27, -36.12) * mm});
            skLineSegment(sketch, "E111", {"start": v(-1.27, 14.68) * mm, "end": v(-21.8, 14.68) * mm});
            skLineSegment(sketch, "E112", {"start": v(-21.8, 14.68) * mm, "end": v(-1.27, -5.86) * mm});
            skLineSegment(sketch, "E113", {"start": v(-1.27, -5.86) * mm, "end": v(-1.27, 14.68) * mm});
            skLineSegment(sketch, "E114", {"start": v(-1.27, -36.12) * mm, "end": v(-21.8, -36.12) * mm});
            skLineSegment(sketch, "E115", {"start": v(-21.8, -36.12) * mm, "end": v(-1.27, -15.59) * mm});
            skLineSegment(sketch, "E116", {"start": v(-1.27, -15.59) * mm, "end": v(-1.27, -36.12) * mm});
            skLineSegment(sketch, "E117", {"start": v(1.27, -25.92) * mm, "end": v(19.03, -25.92) * mm});
            skLineSegment(sketch, "E118", {"start": v(1.27, -33.58) * mm, "end": v(19.03, -33.58) * mm});
            skArc(sketch, "E119", {"start": v(19.03, -25.92) * mm, "mid": v(22.86, -29.75) * mm, "end": v(19.03, -33.58) * mm});
            skLineSegment(sketch, "E120", {"start": v(-22.86, 12.14) * mm, "end": v(-22.86, -33.58) * mm});
            skLineSegment(sketch, "E121", {"start": v(-22.86, -33.58) * mm, "end": v(-25.4, -36.12) * mm});
            skLineSegment(sketch, "E122", {"start": v(-25.4, 14.68) * mm, "end": v(-22.86, 12.14) * mm});
            skLineSegment(sketch, "E123", {"start": v(25.4, 8.3) * mm, "end": v(25.73, -9.45) * mm});
            skLineSegment(sketch, "E124", {"start": v(25.73, -12) * mm, "end": v(25.4, -29.81) * mm});
            skPoint(sketch, "E124.endSnap0", {"position": v(25.4, -29.75) * mm});
            skLineSegment(sketch, "E125.MirrorCS", {"start": v(1.27, 4.47) * mm, "end": v(19.03, 4.47) * mm});
            skLineSegment(sketch, "E126.MirrorCS", {"start": v(1.27, 12.14) * mm, "end": v(19.03, 12.14) * mm});
            skArc(sketch, "E127.MirrorCS", {"start": v(19.03, 4.47) * mm, "mid": v(22.86, 8.3) * mm, "end": v(19.03, 12.14) * mm});
            skLineSegment(sketch, "E128.bottom", {"start": v(-34.3, 23.57) * mm, "end": v(34.3, 23.57) * mm});
            skLineSegment(sketch, "E128.top", {"start": v(-34.3, -45.01) * mm, "end": v(34.3, -45.01) * mm});
            skLineSegment(sketch, "E128.left", {"start": v(-34.3, 23.57) * mm, "end": v(-34.3, -45.01) * mm});
            skLineSegment(sketch, "E128.right", {"start": v(34.3, 23.57) * mm, "end": v(34.29, -45.01) * mm});
            skLineSegment(sketch, "E129", {"start": v(-21.8, 14.68) * mm, "end": v(-25.4, 14.68) * mm});
            skLineSegment(sketch, "E130", {"start": v(-21.8, -36.12) * mm, "end": v(-25.4, -36.12) * mm});
            skSolve(sketch);
        }
        {
            var Q0;
            {var subQ1=sQuery(id+"F28.wireOp",EDGE,"E112");Q0=makeQuery(id+"F28.imprint","IMPRINT",FACE,{"disambiguationData":[TD([[makeQuery(id+"F28.imprint","IMPRINT",EDGE,{"derivedFrom":subQ1}),-1.0]])]});}
            var Q1;
            Q1=makeQuery(id+"F28.imprint","IMPRINT",FACE,{"disambiguationData":[TD([[makeQuery(id+"F28.imprint","IMPRINT",EDGE,{"derivedFrom":sQuery(id+"F28.wireOp",EDGE,"E109.MirrorCS")}),-1.0]])]});
            var Q2;
            {var subQ6=sQuery(id+"F28.wireOp",EDGE,"E98");Q2=makeQuery(id+"F28.imprint","IMPRINT",FACE,{"disambiguationData":[TD([[makeQuery(id+"F28.imprint","IMPRINT",EDGE,{"derivedFrom":subQ6}),1.0]])]});}
            var Q3;
            Q3=makeQuery(id+"F28.imprint","IMPRINT",FACE,{"disambiguationData":[TD([[makeQuery(id+"F28.imprint","IMPRINT",EDGE,{"derivedFrom":sQuery(id+"F28.wireOp",EDGE,"E110.MirrorCS")}),-1.0]])]});
            var Q4;
            {var subQ1=sQuery(id+"F28.wireOp",EDGE,"E115");Q4=makeQuery(id+"F28.imprint","IMPRINT",FACE,{"disambiguationData":[TD([[makeQuery(id+"F28.imprint","IMPRINT",EDGE,{"derivedFrom":subQ1}),1.0]])]});}
            var Q5;
            {var subQ0=sQuery(id+"F28.wireOp",EDGE,"E103");Q5=makeQuery(id+"F28.imprint","IMPRINT",FACE,{"disambiguationData":[TD([[makeQuery(id+"F28.imprint","IMPRINT",EDGE,{"derivedFrom":subQ0}),-1.0]])]});}
            extrude(context, id + "F29", {"entities" : qUnion([Q0, Q1, Q2, Q3, Q4, Q5]), "operationType" : NewBodyOperationType.REMOVE, "oppositeDirection" : true, "depth" : 2.54 * mm, "offsetDistance" : 25.4 * mm});
        }
        {
            var Q0;
            {var subQ0=sQuery(id+"F28.wireOp",EDGE,"E97");var subQ3=sQuery(id+"F28.wireOp",EDGE,"E120");var subQ4=makeQuery(id+"F28.imprint","INTERSECT",VERTEX,{"derivedFrom":[subQ0,subQ3]});Q0=makeQuery(id+"F28.imprint","IMPRINT",FACE,{"disambiguationData":[TD([[makeQuery(id+"F28.imprint","IMPRINT",EDGE,{"disambiguationData":[TD([[subQ4,1.0]])],"derivedFrom":subQ3}),1.0]])]});}
            var Q1;
            {var subQ0=sQuery(id+"F28.wireOp",EDGE,"E100");var subQ3=sQuery(id+"F28.wireOp",EDGE,"E120");var subQ4=makeQuery(id+"F28.imprint","INTERSECT",VERTEX,{"derivedFrom":[subQ0,subQ3]});Q1=makeQuery(id+"F28.imprint","IMPRINT",FACE,{"disambiguationData":[TD([[makeQuery(id+"F28.imprint","IMPRINT",EDGE,{"disambiguationData":[TD([[subQ4,-1.0]])],"derivedFrom":subQ3}),1.0]])]});}
            var Q2;
            {var subQ0=sQuery(id+"F28.wireOp",EDGE,"E125.MirrorCS");Q2=makeQuery(id+"F28.imprint","IMPRINT",FACE,{"disambiguationData":[TD([[makeQuery(id+"F28.imprint","IMPRINT",EDGE,{"derivedFrom":subQ0}),1.0]])]});}
            var Q3;
            {var subQ0=sQuery(id+"F28.wireOp",EDGE,"E117");Q3=makeQuery(id+"F28.imprint","IMPRINT",FACE,{"disambiguationData":[TD([[makeQuery(id+"F28.imprint","IMPRINT",EDGE,{"derivedFrom":subQ0}),-1.0]])]});}
            extrude(context, id + "F30", {"entities" : qUnion([Q0, Q1, Q2, Q3]), "depth" : 2.54 * mm, "offsetDistance" : 25.4 * mm});
        }
        {
            var Q0;
            Q0=makeQuery(id+"F27.opExtrude","CAP_EDGE",EDGE,{"disambiguationData":[OSD([sQuery(id+"F26.wireOp",EDGE,"E85.left")])],"isStart":false});
            var Q1;
            Q1=makeQuery(id+"F27.opExtrude","CAP_EDGE",EDGE,{"disambiguationData":[OSD([sQuery(id+"F26.wireOp",EDGE,"E85.top")])],"isStart":false});
            var Q2;
            Q2=makeQuery(id+"F27.opExtrude","CAP_EDGE",EDGE,{"disambiguationData":[OSD([sQuery(id+"F26.wireOp",EDGE,"E85.right")])],"isStart":false});
            var Q3;
            Q3=makeQuery(id+"F27.opExtrude","CAP_EDGE",EDGE,{"disambiguationData":[OSD([sQuery(id+"F26.wireOp",EDGE,"E85.bottom")])],"isStart":false});
            chamfer(context, id + "F31", {"entities" : qUnion([Q0, Q1, Q2, Q3]), "width" : 2.54 * mm, "tangentPropagation" : true});
        }
    });
